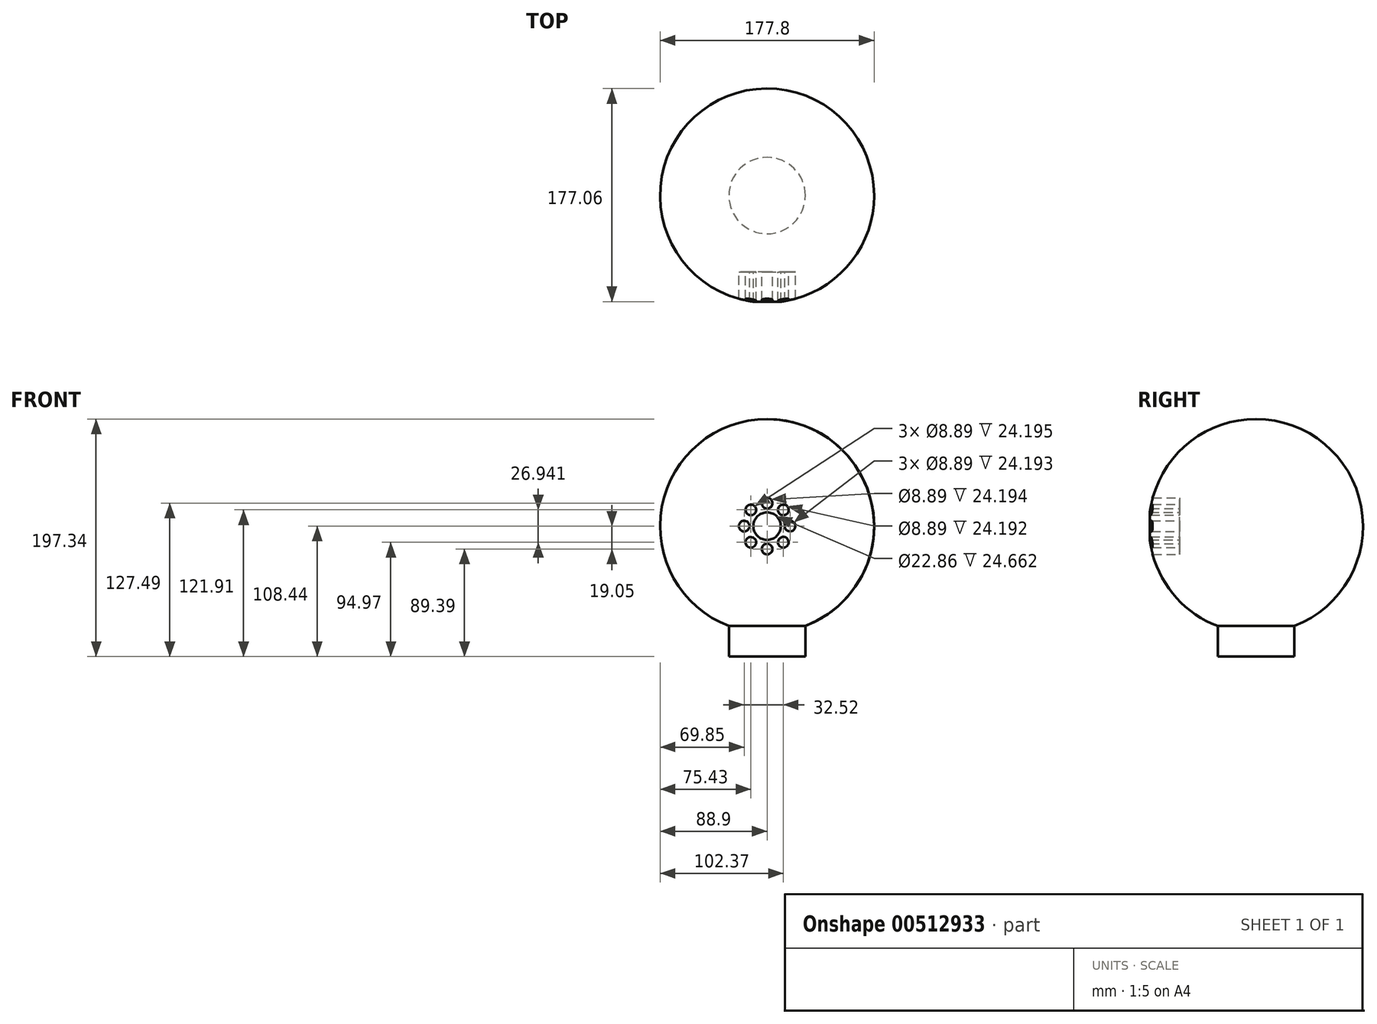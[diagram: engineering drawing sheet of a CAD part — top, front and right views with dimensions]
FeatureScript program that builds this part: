
annotation { "Feature Type Name" : "Feature", "Feature Type Description" : "" }
export const myFeature = defineFeature(function(context is Context, id is Id, definition is map)
    precondition{}
    {
        {
            var Q0;
            Q0=qCreatedBy(makeId("Front.planeOp"),FACE);
            var sketch = newSketch(context, id + "F0", { "sketchPlane" : qUnion([Q0])});
            skArc(sketch, "E0", {"start": v(31.75, -83.04) * mm, "mid": v(87.42, 16.14) * mm, "end": v(0, 88.9) * mm});
            skLineSegment(sketch, "E1", {"start": v(0, 88.9) * mm, "end": v(0, -83.04) * mm});
            skLineSegment(sketch, "E2", {"start": v(31.75, -83.04) * mm, "end": v(31.75, -108.44) * mm});
            skLineSegment(sketch, "E3", {"start": v(31.75, -108.44) * mm, "end": v(0, -108.44) * mm});
            skLineSegment(sketch, "E4", {"start": v(0, -108.44) * mm, "end": v(0, -83.04) * mm});
            skLineSegment(sketch, "E5", {"start": v(0, -83.04) * mm, "end": v(31.75, -83.04) * mm, "construction": true});
            skSolve(sketch);
        }
        {
            var Q0;
            Q0=makeQuery(id+"F0.imprint","IMPRINT",FACE,{"disambiguationData":[TD([[makeQuery(id+"F0.imprint","IMPRINT",EDGE,{"derivedFrom":sQuery(id+"F0.wireOp",EDGE,"E0")}),1.0]])]});
            var Q1;
            Q1=sQuery(id+"F0.wireOp",EDGE,"E1");
            revolve(context, id + "F1", {"entities" : qUnion([Q0]), "axis" : qUnion([Q1]), "revolveType" : RevolveType.FULL});
        }
        {
            var Q0;
            Q0=qCreatedBy(makeId("Front.planeOp"),FACE);
            cPlane(context, id + "F2", {"entities" : qUnion([Q0]), "cplaneType" : CPlaneType.OFFSET, "offset" : 63.5 * mm, "width" : 152.4 * mm, "height" : 152.4 * mm});
        }
        {
            var Q0;
            Q0=qCreatedBy(id+"F2.planeOp",FACE);
            var sketch = newSketch(context, id + "F3", { "sketchPlane" : qUnion([Q0])});
            skCircle(sketch, "E6", {"center": v(0, 0) * mm, "radius": 11.43 * mm});
            skCircle(sketch, "E7", {"center": v(0, 19.05) * mm, "radius": 4.45 * mm});
            skCircle(sketch, "E8", {"center": v(0, -19.05) * mm, "radius": 4.45 * mm});
            skCircle(sketch, "E9", {"center": v(19.05, 0) * mm, "radius": 4.45 * mm});
            skCircle(sketch, "E10", {"center": v(-19.05, 0) * mm, "radius": 4.45 * mm});
            skCircle(sketch, "E11", {"center": v(0, 0) * mm, "radius": 19.05 * mm, "construction": true});
            skCircle(sketch, "E12", {"center": v(-13.47, 13.47) * mm, "radius": 4.45 * mm});
            skCircle(sketch, "E13", {"center": v(13.47, 13.47) * mm, "radius": 4.45 * mm});
            skCircle(sketch, "E14", {"center": v(13.47, -13.47) * mm, "radius": 4.45 * mm});
            skCircle(sketch, "E15", {"center": v(-13.47, -13.47) * mm, "radius": 4.45 * mm});
            skLineSegment(sketch, "E16", {"start": v(0, 0) * mm, "end": v(0, 19.05) * mm, "construction": true});
            skLineSegment(sketch, "E17", {"start": v(0, 0) * mm, "end": v(19.05, 0) * mm});
            skLineSegment(sketch, "E18", {"start": v(0, 0) * mm, "end": v(13.47, -13.47) * mm, "construction": true});
            skLineSegment(sketch, "E19", {"start": v(0, 0) * mm, "end": v(13.47, 13.47) * mm, "construction": true});
            skLineSegment(sketch, "E20", {"start": v(0, 0) * mm, "end": v(-13.47, 13.47) * mm, "construction": true});
            skLineSegment(sketch, "E21", {"start": v(0, 0) * mm, "end": v(-13.47, -13.47) * mm, "construction": true});
            skLineSegment(sketch, "E22", {"start": v(0, 0) * mm, "end": v(0, -19.05) * mm, "construction": true});
            skLineSegment(sketch, "E23", {"start": v(0, 0) * mm, "end": v(-19.05, 0) * mm});
            skSolve(sketch);
        }
        {
            var Q0;
            Q0=qSketchRegion(id+"F3",true);
            extrude(context, id + "F4", {"entities" : qUnion([Q0]), "operationType" : NewBodyOperationType.REMOVE, "depth" : 76.2 * mm});
        }
    });
